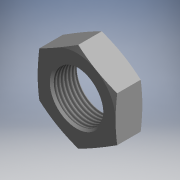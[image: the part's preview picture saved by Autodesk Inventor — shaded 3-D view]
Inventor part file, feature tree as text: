
AUTODESK INVENTOR PART (.ipt)
format: ipt  version: 2017.3 (Build 213256000, 256)  size: 128,000 bytes
history: native  units: mm (DEFAULTED — no unit token found)
features: other x14, sketch x3, revolve x2, extrude x1, thread x1
ambient origin geometry x8: Origin, YZ Plane, XZ Plane, XY Plane, X Axis, Y Axis, Z Axis, Center Point
bodies: Solid1 (feature_tree)
feature tree (21):
  revolve  "Revolution1"  [1 undecoded]
  extrude  "Extrusion1"  Depth=9.376mm TaperAngle=0.0deg
  revolve  "Revolution2"  [1 undecoded]
  thread  "Thread1"  [1 undecoded]
  other  "2CYL_XY"
  other  "2CYL_YZ"
  other  "2CYL_ZX"
  other  "2CYL_X"
  other  "2CYL_Y"
  other  "2CYL_Z"
  other  "2CYL_Center"
  other  "din439b_punkt_XY"
  other  "din439b_punkt_YZ"
  other  "din439b_punkt_ZX"
  other  "din439b_punkt_X"
  other  "din439b_punkt_Y"
  other  "din439b_punkt_Z"
  other  "din439b_punkt_Center"
  sketch  "Sketch_1"  dims[d0=360.0deg d1=24.0mm d2=0.0mm]
  sketch  "Sketch_2"  dims[d3=360.0deg d4=9.376mm d5=0.0mm]
  sketch  "Sketch_3"  dims[d6=0.0mm]
note: 3 required parameter values undecoded (feature->parameter linkage not recoverable at this tier; creation-order binding heuristic only, values carry confidence <= 0.55)